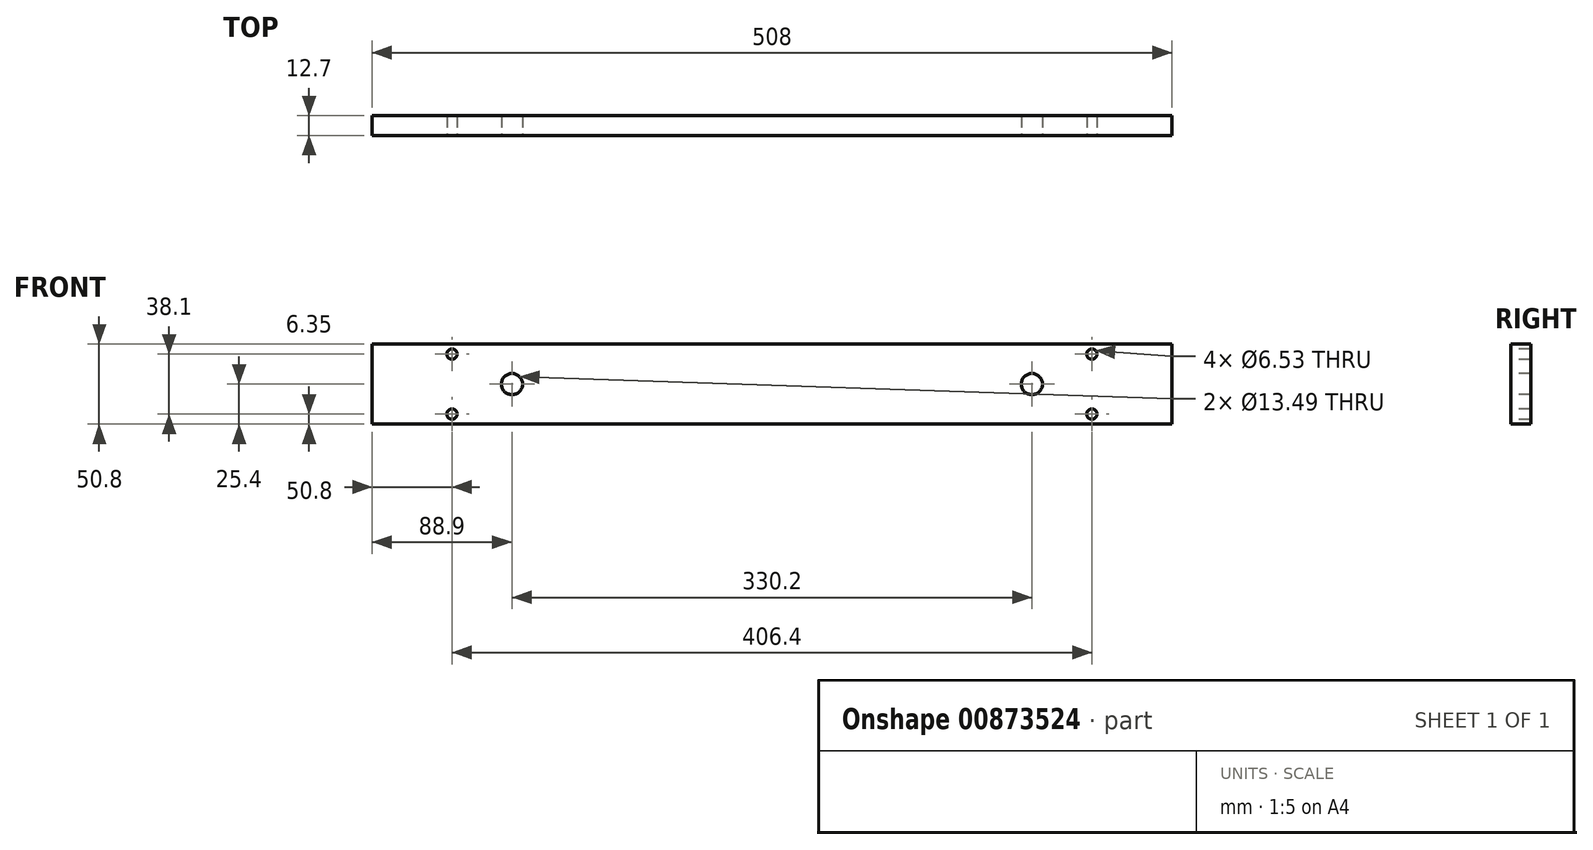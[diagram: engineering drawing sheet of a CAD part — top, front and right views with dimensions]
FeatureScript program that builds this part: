
annotation { "Feature Type Name" : "Feature", "Feature Type Description" : "" }
export const myFeature = defineFeature(function(context is Context, id is Id, definition is map)
    precondition{}
    {
        {
            var Q0;
            Q0=qCreatedBy(makeId("Front.planeOp"),FACE);
            var sketch = newSketch(context, id + "F0", { "sketchPlane" : qUnion([Q0])});
            skLineSegment(sketch, "E0.bottom", {"start": v(254, -25.4) * mm, "end": v(-254, -25.4) * mm});
            skLineSegment(sketch, "E0.top", {"start": v(254, 25.4) * mm, "end": v(-254, 25.4) * mm});
            skLineSegment(sketch, "E0.left", {"start": v(254, -25.4) * mm, "end": v(254, 25.4) * mm});
            skLineSegment(sketch, "E0.right", {"start": v(-254, -25.4) * mm, "end": v(-254, 25.4) * mm});
            skPoint(sketch, "E0.middle", {"position": v(0, 0) * mm});
            skSolve(sketch);
        }
        {
            var Q0;
            Q0=makeQuery(id+"F0.imprint","IMPRINT",FACE,{"disambiguationData":[TD([[makeQuery(id+"F0.imprint","IMPRINT",EDGE,{"derivedFrom":sQuery(id+"F0.wireOp",EDGE,"E0.bottom")}),-1.0]])]});
            extrude(context, id + "F1", {"entities" : qUnion([Q0]), "depth" : 12.7 * mm, "offsetDistance" : 25.4 * mm});
        }
        {
            var Q0;
            Q0=makeQuery(id+"F1.opExtrude","CAP_FACE",FACE,{"disambiguationData":[OSD([sQuery(id+"F0.wireOp",EDGE,"E0.bottom"),sQuery(id+"F0.wireOp",EDGE,"E0.top"),sQuery(id+"F0.wireOp",EDGE,"E0.left"),sQuery(id+"F0.wireOp",EDGE,"E0.right")])],"isStart":false});
            var sketch = newSketch(context, id + "F2", { "sketchPlane" : qUnion([Q0])});
            skPoint(sketch, "E1", {"position": v(-203.2, 19.05) * mm});
            skPoint(sketch, "E2", {"position": v(203.2, 19.05) * mm});
            skPoint(sketch, "E3", {"position": v(-203.2, -19.05) * mm});
            skPoint(sketch, "E4", {"position": v(203.2, -19.05) * mm});
            skSolve(sketch);
        }
        {
            var Q0;
            Q0=sQuery(id+"F2.wireOp",VERTEX,"E1");
            var Q1;
            Q1=sQuery(id+"F2.wireOp",VERTEX,"E2");
            var Q2;
            Q2=sQuery(id+"F2.wireOp",VERTEX,"E3");
            var Q3;
            Q3=sQuery(id+"F2.wireOp",VERTEX,"E4");
            var Q4;
            Q4=makeQuery(id+"F1.opExtrude","SWEPT_BODY",BODY,{"disambiguationData":[OSD([sQuery(id+"F0.wireOp",EDGE,"E0.bottom"),sQuery(id+"F0.wireOp",EDGE,"E0.top"),sQuery(id+"F0.wireOp",EDGE,"E0.left"),sQuery(id+"F0.wireOp",EDGE,"E0.right")])]});
            hole(context, id + "F3", {"style" : HoleStyle.SIMPLE, "endStyle" : HoleEndStyle.THROUGH, "holeDiameter" : 6.53 * mm, "majorDiameter" : 6.35 * mm, "isTappedThrough" : true, "tappedDepth" : 12.7 * mm, "tapClearance" : 3, "locations" : qUnion([Q0, Q1, Q2, Q3]), "scope" : qUnion([Q4])});
        }
        {
            var Q0;
            Q0=makeQuery(id+"F1.opExtrude","CAP_FACE",FACE,{"disambiguationData":[OSD([sQuery(id+"F0.wireOp",EDGE,"E0.bottom"),sQuery(id+"F0.wireOp",EDGE,"E0.top"),sQuery(id+"F0.wireOp",EDGE,"E0.left"),sQuery(id+"F0.wireOp",EDGE,"E0.right")])],"isStart":false});
            var sketch = newSketch(context, id + "F4", { "sketchPlane" : qUnion([Q0])});
            skPoint(sketch, "E5", {"position": v(-165.1, 0) * mm});
            skPoint(sketch, "E6", {"position": v(165.1, 0) * mm});
            skSolve(sketch);
        }
        {
            var Q0;
            Q0=sQuery(id+"F4.wireOp",VERTEX,"E6");
            var Q1;
            Q1=sQuery(id+"F4.wireOp",VERTEX,"E5");
            var Q2;
            Q2=makeQuery(id+"F1.opExtrude","SWEPT_BODY",BODY,{"disambiguationData":[OSD([sQuery(id+"F0.wireOp",EDGE,"E0.bottom"),sQuery(id+"F0.wireOp",EDGE,"E0.top"),sQuery(id+"F0.wireOp",EDGE,"E0.left"),sQuery(id+"F0.wireOp",EDGE,"E0.right")])]});
            hole(context, id + "F5", {"style" : HoleStyle.SIMPLE, "endStyle" : HoleEndStyle.THROUGH, "standardTappedOrClearance" : lookupTablePath({ "fit" : "Free", "standard" : "ANSI", "size" : "1/2", "type" : "Clearance" }), "standardBlindInLast" : lookupTablePath({ "fit" : "Free", "standard" : "ANSI", "engagement" : "75%", "pitch" : "13 tpi", "size" : "1/2", "type" : "Clearance & tapped" }), "holeDiameter" : 13.5 * mm, "majorDiameter" : 12.7 * mm, "isTappedThrough" : true, "tappedDepth" : 12.7 * mm, "tapClearance" : 3, "locations" : qUnion([Q0, Q1]), "scope" : qUnion([Q2])});
        }
    });
